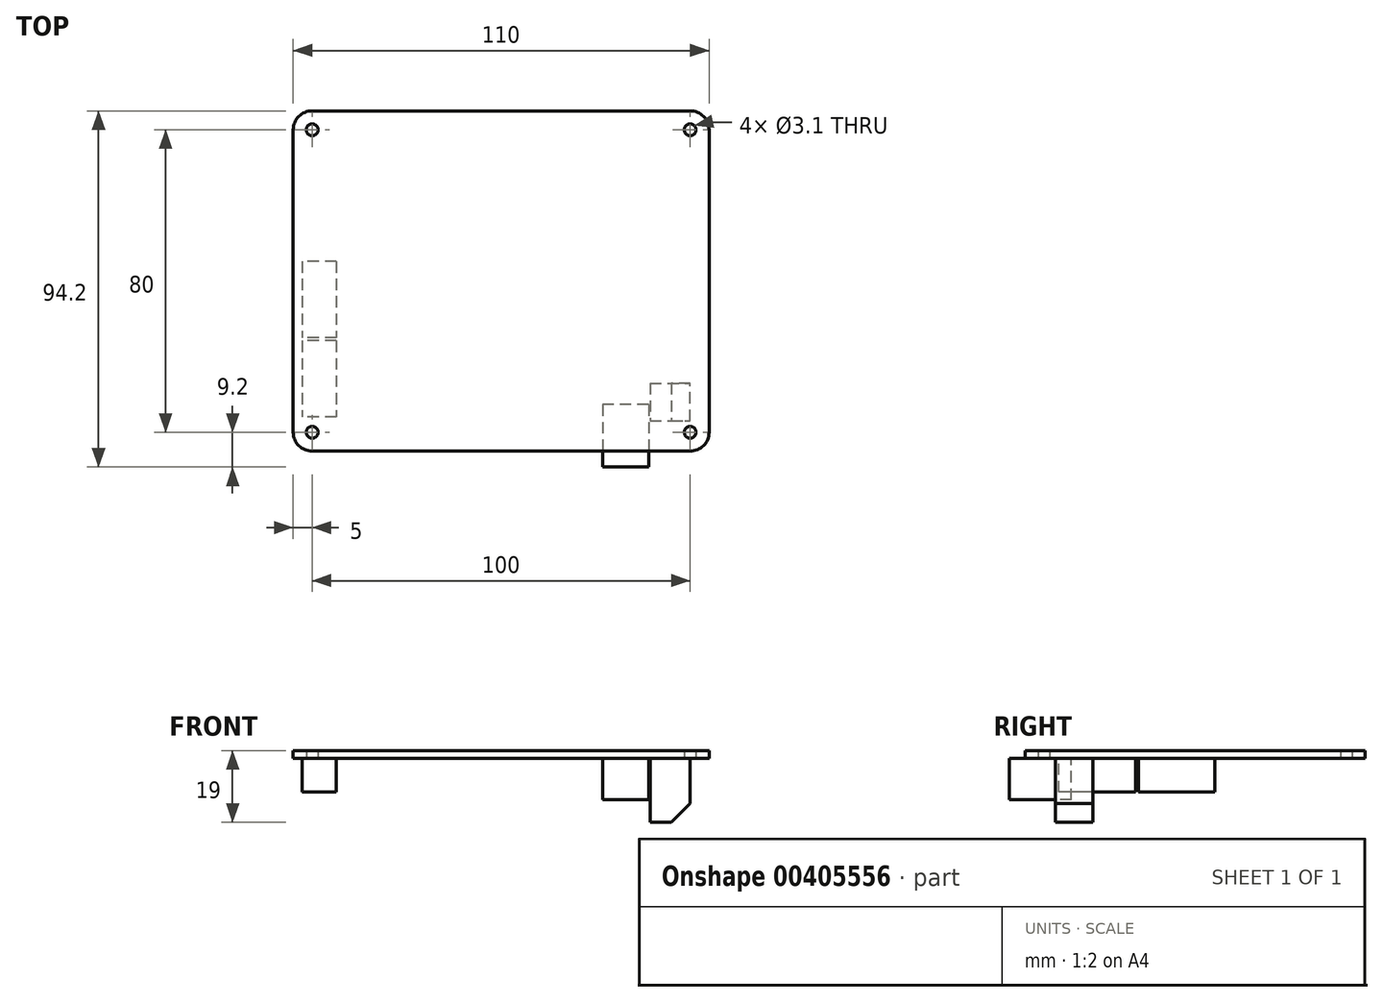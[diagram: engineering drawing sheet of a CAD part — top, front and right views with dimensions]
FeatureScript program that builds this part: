
annotation { "Feature Type Name" : "Feature", "Feature Type Description" : "" }
export const myFeature = defineFeature(function(context is Context, id is Id, definition is map)
    precondition{}
    {
        {
            var Q0;
            Q0=qCreatedBy(makeId("Top.planeOp"),FACE);
            var sketch = newSketch(context, id + "F0", { "sketchPlane" : qUnion([Q0])});
            skLineSegment(sketch, "E0.rect.bottom", {"start": v(-50, 40) * mm, "end": v(50, 40) * mm, "construction": true});
            skLineSegment(sketch, "E0.rect.top", {"start": v(-50, -40) * mm, "end": v(50, -40) * mm, "construction": true});
            skLineSegment(sketch, "E0.rect.left", {"start": v(-50, 40) * mm, "end": v(-50, -40) * mm, "construction": true});
            skLineSegment(sketch, "E0.rect.right", {"start": v(50, 40) * mm, "end": v(50, -40) * mm, "construction": true});
            skPoint(sketch, "E0.rect.middle", {"position": v(0, 0) * mm});
            skCircle(sketch, "E1", {"center": v(-50, 40) * mm, "radius": 1.55 * mm});
            skCircle(sketch, "E2", {"center": v(50, 40) * mm, "radius": 1.55 * mm});
            skCircle(sketch, "E3", {"center": v(50, -40) * mm, "radius": 1.55 * mm});
            skCircle(sketch, "E4", {"center": v(-50, -40) * mm, "radius": 1.55 * mm});
            skLineSegment(sketch, "E5.rect.bottom", {"start": v(-50, 45) * mm, "end": v(50, 45) * mm});
            skLineSegment(sketch, "E5.rect.top", {"start": v(-50, -45) * mm, "end": v(50, -45) * mm});
            skLineSegment(sketch, "E5.rect.left", {"start": v(-55, 40) * mm, "end": v(-55, -40) * mm});
            skLineSegment(sketch, "E5.rect.right", {"start": v(55, 40) * mm, "end": v(55, -40) * mm});
            skPoint(sketch, "E6.visualSharp", {"position": v(-55, 45) * mm});
            skArc(sketch, "E6.filletArc", {"start": v(-50, 45) * mm, "mid": v(-53.54, 43.54) * mm, "end": v(-55, 40) * mm});
            skPoint(sketch, "E7.visualSharp", {"position": v(55, 45) * mm});
            skArc(sketch, "E7.filletArc", {"start": v(55, 40) * mm, "mid": v(53.54, 43.54) * mm, "end": v(50, 45) * mm});
            skPoint(sketch, "E8.visualSharp", {"position": v(55, -45) * mm});
            skArc(sketch, "E8.filletArc", {"start": v(50, -45) * mm, "mid": v(53.54, -43.54) * mm, "end": v(55, -40) * mm});
            skPoint(sketch, "E9.visualSharp", {"position": v(-55, -45) * mm});
            skArc(sketch, "E9.filletArc", {"start": v(-55, -40) * mm, "mid": v(-53.54, -43.54) * mm, "end": v(-50, -45) * mm});
            skSolve(sketch);
        }
        {
            var Q0;
            Q0=qSketchRegion(id+"F0",true);
            extrude(context, id + "F1", {"entities" : qUnion([Q0]), "depth" : 2 * mm});
        }
        {
            var Q0;
            Q0=qCreatedBy(makeId("Top.planeOp"),FACE);
            var sketch = newSketch(context, id + "F2", { "sketchPlane" : qUnion([Q0])});
            skLineSegment(sketch, "E10.bottom", {"start": v(39.4, -27) * mm, "end": v(55, -27) * mm});
            skLineSegment(sketch, "E10.top", {"start": v(39.4, -37) * mm, "end": v(55, -37) * mm});
            skLineSegment(sketch, "E10.left", {"start": v(39.4, -27) * mm, "end": v(39.4, -37) * mm});
            skLineSegment(sketch, "E10.right", {"start": v(55, -27) * mm, "end": v(55, -37) * mm});
            skLineSegment(sketch, "E11.bottom", {"start": v(39, -32.7) * mm, "end": v(26.8, -32.7) * mm});
            skLineSegment(sketch, "E11.top", {"start": v(39, -49.2) * mm, "end": v(26.8, -49.2) * mm});
            skLineSegment(sketch, "E11.left", {"start": v(39, -32.7) * mm, "end": v(39, -49.2) * mm});
            skLineSegment(sketch, "E11.right", {"start": v(26.8, -32.7) * mm, "end": v(26.8, -49.2) * mm});
            skLineSegment(sketch, "E12.bottom", {"start": v(-43.6, 5.2) * mm, "end": v(-52.6, 5.2) * mm});
            skLineSegment(sketch, "E12.top", {"start": v(-43.6, -15) * mm, "end": v(-52.6, -15) * mm});
            skLineSegment(sketch, "E12.left", {"start": v(-43.6, 5.2) * mm, "end": v(-43.6, -15) * mm});
            skLineSegment(sketch, "E12.right", {"start": v(-52.6, 5.2) * mm, "end": v(-52.6, -15) * mm});
            skLineSegment(sketch, "E13.bottom", {"start": v(-43.6, -15.8) * mm, "end": v(-52.6, -15.8) * mm});
            skLineSegment(sketch, "E13.top", {"start": v(-43.6, -36) * mm, "end": v(-52.6, -36) * mm});
            skLineSegment(sketch, "E13.left", {"start": v(-43.6, -15.8) * mm, "end": v(-43.6, -36) * mm});
            skLineSegment(sketch, "E13.right", {"start": v(-52.6, -15.8) * mm, "end": v(-52.6, -36) * mm});
            skLineSegment(sketch, "E14.0", {"start": v(-50, -45) * mm, "end": v(50, -45) * mm, "construction": true});
            skArc(sketch, "E14.1", {"start": v(50, -45) * mm, "mid": v(53.54, -43.54) * mm, "end": v(55, -40) * mm, "construction": true});
            skLineSegment(sketch, "E14.2", {"start": v(55, 40) * mm, "end": v(55, -40) * mm, "construction": true});
            skArc(sketch, "E14.3", {"start": v(55, 40) * mm, "mid": v(53.54, 43.54) * mm, "end": v(50, 45) * mm, "construction": true});
            skLineSegment(sketch, "E14.4", {"start": v(-50, 45) * mm, "end": v(50, 45) * mm, "construction": true});
            skArc(sketch, "E14.5", {"start": v(-50, 45) * mm, "mid": v(-53.54, 43.54) * mm, "end": v(-55, 40) * mm, "construction": true});
            skLineSegment(sketch, "E14.6", {"start": v(-55, 40) * mm, "end": v(-55, -40) * mm, "construction": true});
            skArc(sketch, "E14.7", {"start": v(-55, -40) * mm, "mid": v(-53.54, -43.54) * mm, "end": v(-50, -45) * mm, "construction": true});
            skLineSegment(sketch, "E15", {"start": v(50, -37) * mm, "end": v(50, -27) * mm});
            skSolve(sketch);
        }
        {
            var Q0;
            {var subQ0=sQuery(id+"F2.wireOp",EDGE,"E11.bottom");Q0=makeQuery(id+"F2.imprint","IMPRINT",FACE,{"disambiguationData":[TD([[makeQuery(id+"F2.imprint","IMPRINT",EDGE,{"derivedFrom":subQ0}),1.0]])]});}
            var Q1;
            {var subQ0=sQuery(id+"F2.wireOp",EDGE,"E11.top");Q1=makeQuery(id+"F2.imprint","IMPRINT",FACE,{"disambiguationData":[TD([[makeQuery(id+"F2.imprint","IMPRINT",EDGE,{"derivedFrom":subQ0}),-1.0]])]});}
            extrude(context, id + "F3", {"entities" : qUnion([Q0, Q1]), "operationType" : NewBodyOperationType.ADD, "oppositeDirection" : true, "depth" : 11 * mm});
        }
        {
            var Q0;
            {var subQ0=sQuery(id+"F2.wireOp",EDGE,"E10.left");Q0=makeQuery(id+"F2.imprint","IMPRINT",FACE,{"disambiguationData":[TD([[makeQuery(id+"F2.imprint","IMPRINT",EDGE,{"derivedFrom":subQ0}),1.0]])]});}
            extrude(context, id + "F4", {"entities" : qUnion([Q0]), "operationType" : NewBodyOperationType.ADD, "oppositeDirection" : true, "depth" : 17 * mm});
        }
        {
            var Q0;
            Q0=makeQuery(id+"F4.opExtrude","CAP_EDGE",EDGE,{"disambiguationData":[OSD([sQuery(id+"F2.wireOp",EDGE,"E15")])],"isStart":false});
            chamfer(context, id + "F5", {"entities" : qUnion([Q0]), "width" : 5 * mm, "tangentPropagation" : true});
        }
        {
            var Q0;
            Q0=makeQuery(id+"F2.imprint","IMPRINT",FACE,{"disambiguationData":[TD([[makeQuery(id+"F2.imprint","IMPRINT",EDGE,{"derivedFrom":sQuery(id+"F2.wireOp",EDGE,"E13.bottom")}),1.0]])]});
            var Q1;
            Q1=makeQuery(id+"F2.imprint","IMPRINT",FACE,{"disambiguationData":[TD([[makeQuery(id+"F2.imprint","IMPRINT",EDGE,{"derivedFrom":sQuery(id+"F2.wireOp",EDGE,"E12.bottom")}),1.0]])]});
            extrude(context, id + "F6", {"entities" : qUnion([Q0, Q1]), "operationType" : NewBodyOperationType.ADD, "oppositeDirection" : true, "depth" : 9 * mm});
        }
    });
